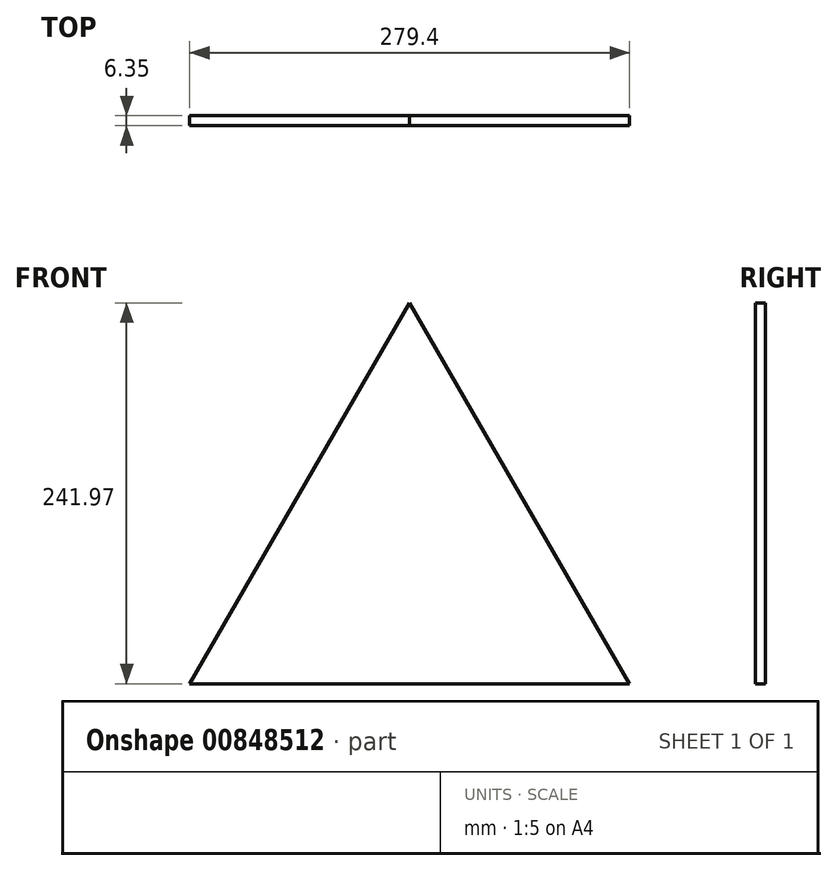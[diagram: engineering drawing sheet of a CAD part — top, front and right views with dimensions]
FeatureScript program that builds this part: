
annotation { "Feature Type Name" : "Feature", "Feature Type Description" : "" }
export const myFeature = defineFeature(function(context is Context, id is Id, definition is map)
    precondition{}
    {
        {
            var Q0;
            Q0=qCreatedBy(makeId("Front.planeOp"),FACE);
            var sketch = newSketch(context, id + "F0", { "sketchPlane" : qUnion([Q0])});
            skLineSegment(sketch, "E0", {"start": v(-139.7, -191.17) * mm, "end": v(0, 50.8) * mm});
            skLineSegment(sketch, "E1", {"start": v(0, 50.8) * mm, "end": v(139.7, -191.17) * mm});
            skLineSegment(sketch, "E2", {"start": v(139.7, -191.17) * mm, "end": v(-139.7, -191.17) * mm});
            skSolve(sketch);
        }
        {
            var Q0;
            Q0=makeQuery(id+"F0.imprint","IMPRINT",FACE,{"disambiguationData":[TD([[makeQuery(id+"F0.imprint","IMPRINT",EDGE,{"derivedFrom":sQuery(id+"F0.wireOp",EDGE,"E0")}),-1.0]])]});
            extrude(context, id + "F1", {"entities" : qUnion([Q0]), "depth" : 6.35 * mm, "offsetDistance" : 25.4 * mm});
        }
    });
